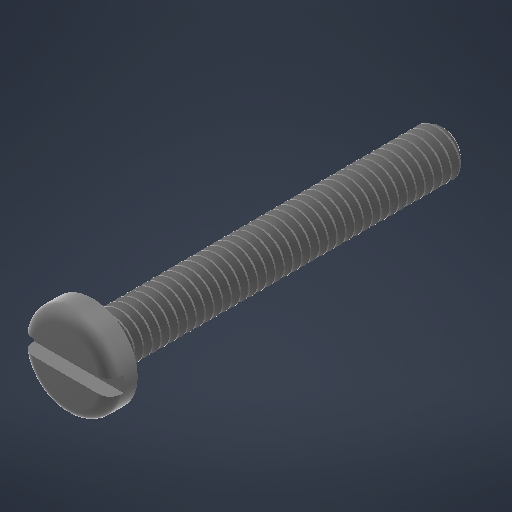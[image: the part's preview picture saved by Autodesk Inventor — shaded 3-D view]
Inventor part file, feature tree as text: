
AUTODESK INVENTOR PART (.ipt)
format: ipt  version: 2025.2 (Build 292293000, 293)  size: 769,024 bytes
history: native  units: in
note: dims shown in document units (in); Inventor stores cm internally (conversion verified against a paired STEP export)
features: other x1, extrude x1
ambient origin geometry x8: Origin, YZ Plane, XZ Plane, XY Plane, X Axis, Y Axis, Z Axis, Center Point
bodies: Solid1 (feature_tree)
feature tree (2):
  other  "Plane1"
  extrude  "Extrude15"  [1 undecoded]
note: 1 required parameter value undecoded (feature->parameter linkage not recoverable at this tier; creation-order binding heuristic only, values carry confidence <= 0.55)
